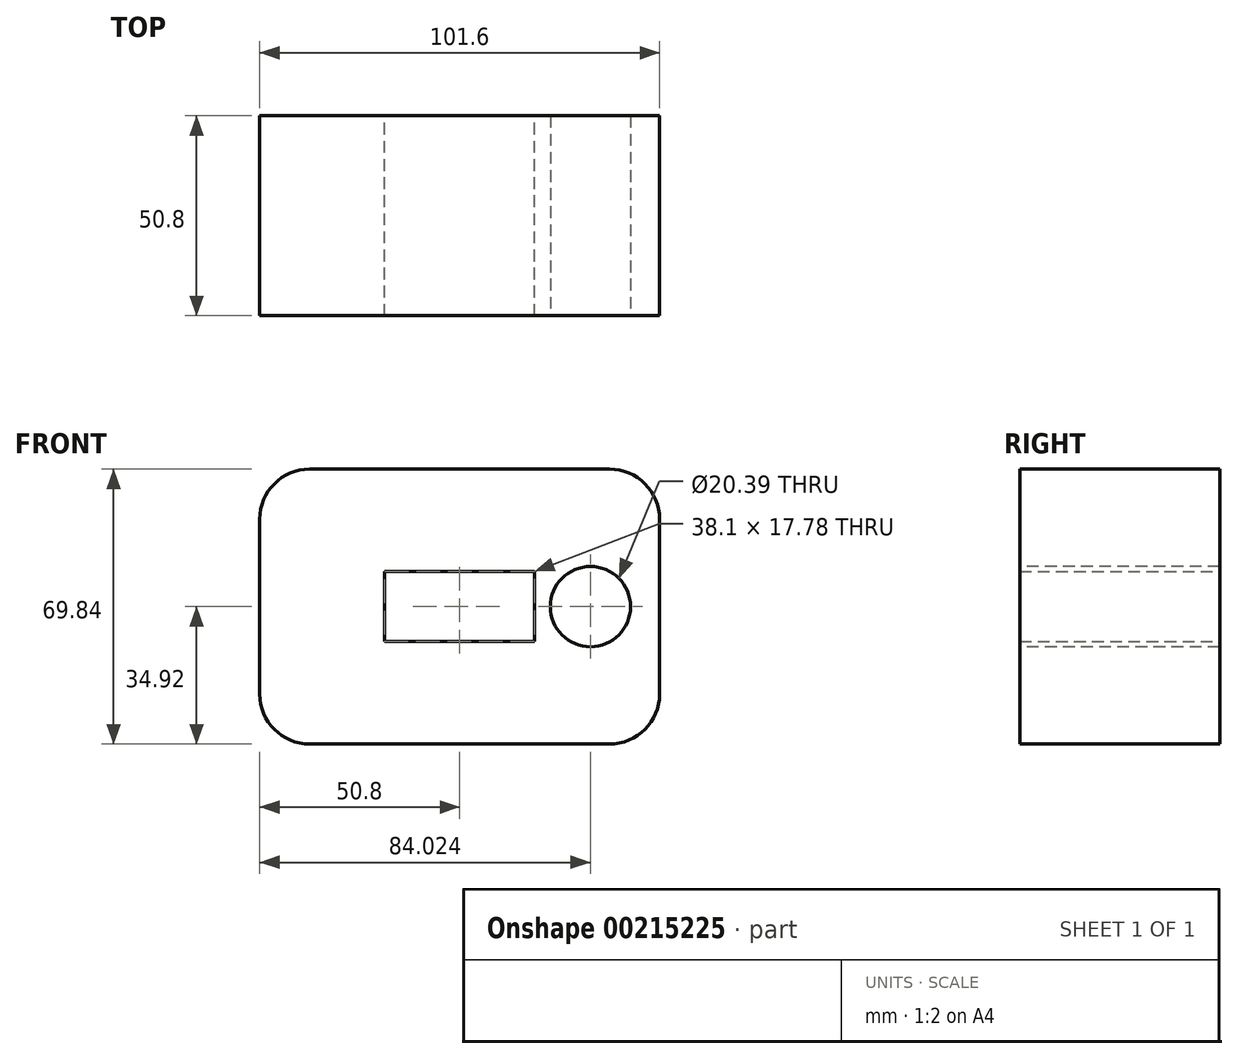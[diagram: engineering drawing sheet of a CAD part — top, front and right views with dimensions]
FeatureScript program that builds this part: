
annotation { "Feature Type Name" : "Feature", "Feature Type Description" : "" }
export const myFeature = defineFeature(function(context is Context, id is Id, definition is map)
    precondition{}
    {
        {
            var Q0;
            Q0=qCreatedBy(makeId("Front.planeOp"),FACE);
            var sketch = newSketch(context, id + "F0", { "sketchPlane" : qUnion([Q0])});
            skLineSegment(sketch, "E0.bottom", {"start": v(50.8, -34.93) * mm, "end": v(-50.8, -34.93) * mm});
            skLineSegment(sketch, "E0.top", {"start": v(50.8, 34.92) * mm, "end": v(-50.8, 34.92) * mm});
            skLineSegment(sketch, "E0.left", {"start": v(50.8, -34.93) * mm, "end": v(50.8, 34.93) * mm});
            skLineSegment(sketch, "E0.right", {"start": v(-50.8, -34.93) * mm, "end": v(-50.8, 34.92) * mm});
            skPoint(sketch, "E0.middle", {"position": v(0, 0) * mm});
            skLineSegment(sketch, "E1.bottom", {"start": v(19.05, -8.9) * mm, "end": v(-19.05, -8.9) * mm});
            skLineSegment(sketch, "E1.top", {"start": v(19.05, 8.9) * mm, "end": v(-19.05, 8.9) * mm});
            skLineSegment(sketch, "E1.left", {"start": v(19.05, -8.9) * mm, "end": v(19.05, 8.9) * mm});
            skLineSegment(sketch, "E1.right", {"start": v(-19.05, -8.9) * mm, "end": v(-19.05, 8.9) * mm});
            skSolve(sketch);
        }
        {
            var Q0;
            Q0=makeQuery(id+"F0.imprint","IMPRINT",FACE,{"disambiguationData":[TD([[makeQuery(id+"F0.imprint","IMPRINT",EDGE,{"derivedFrom":sQuery(id+"F0.wireOp",EDGE,"E0.bottom")}),-1.0]])]});
            extrude(context, id + "F1", {"entities" : qUnion([Q0]), "endBound" : BoundingType.SYMMETRIC, "depth" : 50.8 * mm});
        }
        {
            var Q0;
            Q0=makeQuery(id+"F1.opExtrude","CAP_FACE",FACE,{"disambiguationData":[OSD([sQuery(id+"F0.wireOp",EDGE,"E0.bottom"),sQuery(id+"F0.wireOp",EDGE,"E0.top"),sQuery(id+"F0.wireOp",EDGE,"E0.left"),sQuery(id+"F0.wireOp",EDGE,"E0.right"),sQuery(id+"F0.wireOp",EDGE,"E1.bottom"),sQuery(id+"F0.wireOp",EDGE,"E1.top"),sQuery(id+"F0.wireOp",EDGE,"E1.left"),sQuery(id+"F0.wireOp",EDGE,"E1.right")])],"isStart":false});
            var sketch = newSketch(context, id + "F2", { "sketchPlane" : qUnion([Q0])});
            skCircle(sketch, "E2", {"center": v(33.22, 0) * mm, "radius": 10.2 * mm});
            skPoint(sketch, "E3", {"position": v(19.05, 0) * mm});
            skSolve(sketch);
        }
        {
            var Q0;
            Q0 = qSketchRegion(id + "F2", true);
            extrude(context, id + "F3", {"entities" : qUnion([Q0]), "operationType" : NewBodyOperationType.REMOVE, "endBound" : BoundingType.THROUGH_ALL, "oppositeDirection" : true, "depth" : 25.4 * mm});
        }
        {
            var Q0;
            Q0=makeQuery(id+"F1.opExtrude","SWEPT_EDGE",EDGE,{"disambiguationData":[OSD([sQuery(id+"F0.wireOp",EDGE,"E0.top"),sQuery(id+"F0.wireOp",EDGE,"E0.right")])]});
            var Q1;
            Q1=makeQuery(id+"F1.opExtrude","SWEPT_EDGE",EDGE,{"disambiguationData":[OSD([sQuery(id+"F0.wireOp",EDGE,"E0.top"),sQuery(id+"F0.wireOp",EDGE,"E0.left")])]});
            var Q2;
            Q2=makeQuery(id+"F1.opExtrude","SWEPT_EDGE",EDGE,{"disambiguationData":[OSD([sQuery(id+"F0.wireOp",EDGE,"E0.bottom"),sQuery(id+"F0.wireOp",EDGE,"E0.left")])]});
            var Q3;
            Q3=makeQuery(id+"F1.opExtrude","SWEPT_EDGE",EDGE,{"disambiguationData":[OSD([sQuery(id+"F0.wireOp",EDGE,"E0.bottom"),sQuery(id+"F0.wireOp",EDGE,"E0.right")])]});
            fillet(context, id + "F4", {"entities" : qUnion([Q0, Q1, Q2, Q3]), "radius" : 12.7 * mm, "tangentPropagation" : true, "allowEdgeOverflow" : false});
        }
    });
